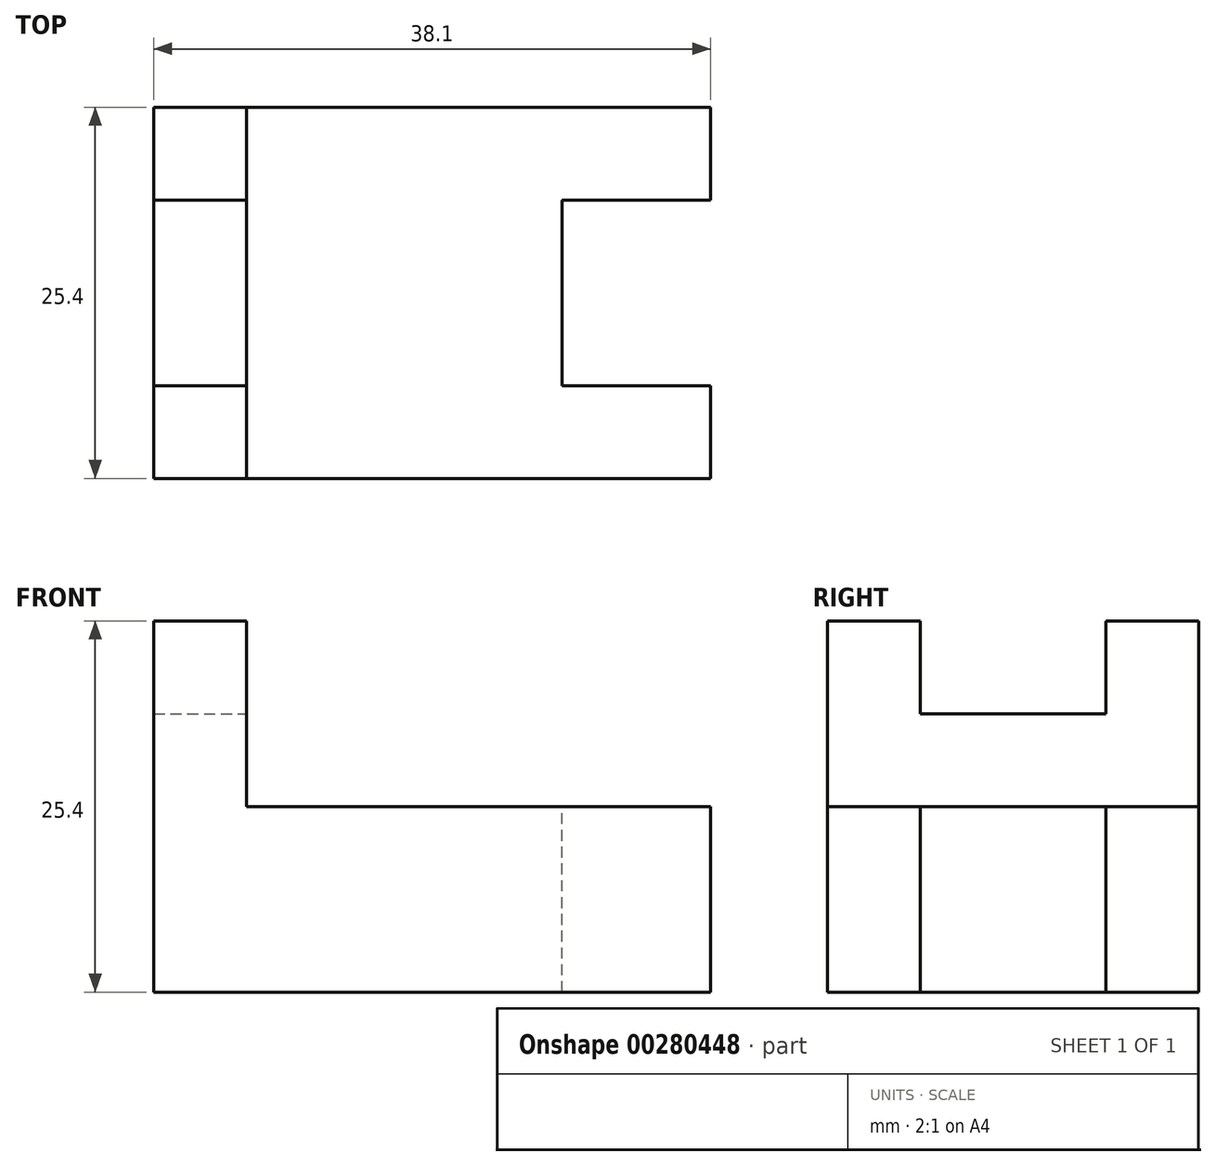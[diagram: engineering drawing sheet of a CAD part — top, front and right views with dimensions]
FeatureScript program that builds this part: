
annotation { "Feature Type Name" : "Feature", "Feature Type Description" : "" }
export const myFeature = defineFeature(function(context is Context, id is Id, definition is map)
    precondition{}
    {
        {
            var Q0;
            Q0=qCreatedBy(makeId("Front.planeOp"),FACE);
            var sketch = newSketch(context, id + "F0", { "sketchPlane" : qUnion([Q0])});
            skLineSegment(sketch, "E0", {"start": v(0, 0) * mm, "end": v(0, 25.4) * mm});
            skLineSegment(sketch, "E1", {"start": v(0, 25.4) * mm, "end": v(6.35, 25.4) * mm});
            skLineSegment(sketch, "E2", {"start": v(6.35, 25.4) * mm, "end": v(6.35, 12.7) * mm});
            skLineSegment(sketch, "E3", {"start": v(6.35, 12.7) * mm, "end": v(38.1, 12.7) * mm});
            skLineSegment(sketch, "E4", {"start": v(38.1, 12.7) * mm, "end": v(38.1, 0) * mm});
            skLineSegment(sketch, "E5", {"start": v(38.1, 0) * mm, "end": v(0, 0) * mm});
            skSolve(sketch);
        }
        {
            var Q0;
            Q0 = qSketchRegion(id + "F0", true);
            extrude(context, id + "F1", {"entities" : qUnion([Q0]), "endBound" : BoundingType.SYMMETRIC, "depth" : 25.4 * mm});
        }
        {
            var Q0;
            Q0=makeQuery(id+"F1.opExtrude","CAP_FACE",FACE,{"disambiguationData":[OSD([sQuery(id+"F0.wireOp",EDGE,"E0"),sQuery(id+"F0.wireOp",EDGE,"E1"),sQuery(id+"F0.wireOp",EDGE,"E2"),sQuery(id+"F0.wireOp",EDGE,"E3"),sQuery(id+"F0.wireOp",EDGE,"E4"),sQuery(id+"F0.wireOp",EDGE,"E5")])],"isStart":false});
            var sketch = newSketch(context, id + "F2", { "sketchPlane" : qUnion([Q0])});
            skLineSegment(sketch, "E6.bottom", {"start": v(38.1, 0) * mm, "end": v(27.94, 0) * mm});
            skLineSegment(sketch, "E6.top", {"start": v(38.1, 12.7) * mm, "end": v(27.94, 12.7) * mm});
            skLineSegment(sketch, "E6.left", {"start": v(38.1, 0) * mm, "end": v(38.1, 12.7) * mm});
            skLineSegment(sketch, "E6.right", {"start": v(27.94, 0) * mm, "end": v(27.94, 12.7) * mm});
            skSolve(sketch);
        }
        {
            var Q0;
            Q0 = qSketchRegion(id + "F2", true);
            extrude(context, id + "F3", {"entities" : qUnion([Q0]), "operationType" : NewBodyOperationType.REMOVE, "oppositeDirection" : true, "depth" : 19.05 * mm, "hasSecondDirection" : true, "secondDirectionOppositeDirection" : true, "secondDirectionDepth" : 6.35 * mm});
        }
        {
            var Q0;
            Q0=makeQuery(id+"F1.opExtrude","CAP_FACE",FACE,{"disambiguationData":[OSD([sQuery(id+"F0.wireOp",EDGE,"E0"),sQuery(id+"F0.wireOp",EDGE,"E1"),sQuery(id+"F0.wireOp",EDGE,"E2"),sQuery(id+"F0.wireOp",EDGE,"E3"),sQuery(id+"F0.wireOp",EDGE,"E4"),sQuery(id+"F0.wireOp",EDGE,"E5")])],"isStart":false});
            var sketch = newSketch(context, id + "F4", { "sketchPlane" : qUnion([Q0])});
            skLineSegment(sketch, "E7.bottom", {"start": v(0, 25.4) * mm, "end": v(6.35, 25.4) * mm});
            skLineSegment(sketch, "E7.top", {"start": v(0, 19.05) * mm, "end": v(6.35, 19.05) * mm});
            skLineSegment(sketch, "E7.left", {"start": v(0, 25.4) * mm, "end": v(0, 19.05) * mm});
            skLineSegment(sketch, "E7.right", {"start": v(6.35, 25.4) * mm, "end": v(6.35, 19.05) * mm});
            skSolve(sketch);
        }
        {
            var Q0;
            Q0 = qSketchRegion(id + "F4", true);
            extrude(context, id + "F5", {"entities" : qUnion([Q0]), "operationType" : NewBodyOperationType.REMOVE, "oppositeDirection" : true, "depth" : 19.05 * mm, "hasSecondDirection" : true, "secondDirectionOppositeDirection" : true, "secondDirectionDepth" : 6.35 * mm});
        }
    });
